# Revit family: Bjælke - LB(B)E
name_source: partatom
category: Structural Framing
units: mm (PartAtom-declared; Revit-internal decimal feet)

## family parameters
Always export as geometry = No
Always vertical = Yes
Cut with Voids When Loaded = No
Material for Model Behavior = Other
OmniClass Number = 23.25.30.11.14.14
OmniClass Title = Beams
Section Shape = Not Defined
Shared = No
Show family pre-cut in plan views = Yes

## types (4) — shared parameters
CRH_RFA_TimeStamp_LastRelease = 20191107
Hylde Højde = 220 mm  [stored 0.721785 ft]
Hylde Højde Maks = 400 mm  [stored 1.31234 ft]
Manufacturer = CRH Concrete

## per-type parameters (varying)
| type | Bredde | Bredde 2 | Bredt Element | Højde | Konsol Tykkelse | Model | Tyk Konsol |
| LBE 50/22/8 | 500 mm  [stored 1.64042 ft] | 170 mm  [stored 0.557743 ft] | No | 300 mm | 80 mm  [stored 0.262467 ft] | LBE | No |
| LBBE 66/22/8 | 660 mm | 240 mm  [stored 0.787402 ft] | Yes | 300 mm | 80 mm  [stored 0.262467 ft] | LBBE | No |
| LBBE 66/22/12 | 660 mm | 240 mm  [stored 0.787402 ft] | Yes | 340 mm  [stored 1.11549 ft] | 120 mm  [stored 0.393701 ft] | LBBE | Yes |
| LBE 50/22/12 | 500 mm  [stored 1.64042 ft] | 170 mm  [stored 0.557743 ft] | No | 340 mm  [stored 1.11549 ft] | 120 mm  [stored 0.393701 ft] | LBE | Yes |

note: [stored X ft] marks values corroborated as IEEE doubles in the binary element streams (Revit-internal decimal feet)

## geometry (parser evidence)
native form markers: Sweep x4
no freeform markers — native parametric forms only
